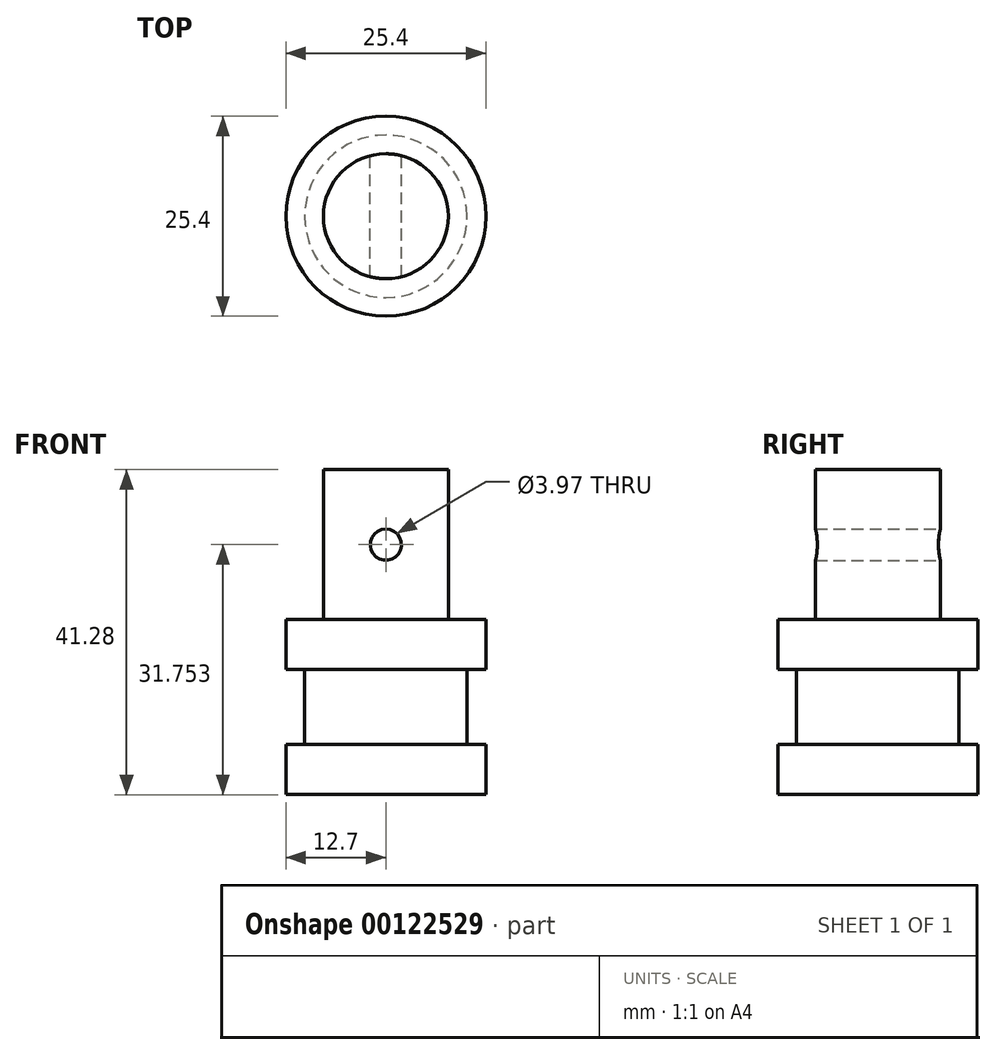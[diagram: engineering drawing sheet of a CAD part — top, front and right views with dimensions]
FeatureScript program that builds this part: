
annotation { "Feature Type Name" : "Feature", "Feature Type Description" : "" }
export const myFeature = defineFeature(function(context is Context, id is Id, definition is map)
    precondition{}
    {
        {
            var Q0;
            Q0=qCreatedBy(makeId("Front.planeOp"),FACE);
            var sketch = newSketch(context, id + "F0", { "sketchPlane" : qUnion([Q0])});
            skLineSegment(sketch, "E0", {"start": v(0, 20.64) * mm, "end": v(0, -20.64) * mm});
            skLineSegment(sketch, "E1", {"start": v(0, -20.64) * mm, "end": v(-12.7, -20.64) * mm});
            skLineSegment(sketch, "E2", {"start": v(-12.7, -20.64) * mm, "end": v(-12.7, -14.29) * mm});
            skLineSegment(sketch, "E3", {"start": v(-12.7, -14.29) * mm, "end": v(-10.32, -14.29) * mm});
            skLineSegment(sketch, "E4", {"start": v(-10.32, -14.29) * mm, "end": v(-10.32, -4.76) * mm});
            skLineSegment(sketch, "E5", {"start": v(-10.32, -4.76) * mm, "end": v(-12.7, -4.76) * mm});
            skLineSegment(sketch, "E6", {"start": v(-12.7, -4.76) * mm, "end": v(-12.7, 1.59) * mm});
            skLineSegment(sketch, "E7", {"start": v(-12.7, 1.59) * mm, "end": v(-7.94, 1.59) * mm});
            skLineSegment(sketch, "E8", {"start": v(-7.94, 1.59) * mm, "end": v(-7.94, 20.64) * mm});
            skLineSegment(sketch, "E9", {"start": v(-7.94, 20.64) * mm, "end": v(0, 20.64) * mm});
            skPoint(sketch, "E10", {"position": v(0, 0) * mm});
            skSolve(sketch);
        }
        {
            var Q0;
            Q0=makeQuery(id+"F0.imprint","IMPRINT",FACE,{"disambiguationData":[TD([[makeQuery(id+"F0.imprint","IMPRINT",EDGE,{"derivedFrom":sQuery(id+"F0.wireOp",EDGE,"E0")}),-1.0]])]});
            var Q1;
            Q1=sQuery(id+"F0.wireOp",EDGE,"E0");
            revolve(context, id + "F1", {"entities" : qUnion([Q0]), "axis" : qUnion([Q1]), "revolveType" : RevolveType.FULL});
        }
        {
            var Q0;
            Q0=qCreatedBy(makeId("Front.planeOp"),FACE);
            var sketch = newSketch(context, id + "F2", { "sketchPlane" : qUnion([Q0])});
            skLineSegment(sketch, "E11", {"start": v(0, 20.64) * mm, "end": v(0, 11.11) * mm});
            skLineSegment(sketch, "E12", {"start": v(7.94, 20.64) * mm, "end": v(7.94, 1.59) * mm});
            skLineSegment(sketch, "E13", {"start": v(-7.94, 1.59) * mm, "end": v(-7.94, 20.64) * mm});
            skCircle(sketch, "E14", {"center": v(0, 11.11) * mm, "radius": 1.98 * mm});
            skSolve(sketch);
        }
        {
            var Q0;
            Q0 = qSketchRegion(id + "F2", true);
            extrude(context, id + "F3", {"entities" : qUnion([Q0]), "operationType" : NewBodyOperationType.REMOVE, "endBound" : BoundingType.THROUGH_ALL, "depth" : 25.4 * mm, "hasSecondDirection" : true, "secondDirectionBound" : SecondDirectionBoundingType.THROUGH_ALL, "secondDirectionOppositeDirection" : true, "secondDirectionDepth" : 25.4 * mm});
        }
    });
